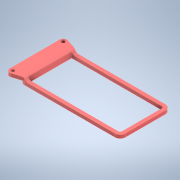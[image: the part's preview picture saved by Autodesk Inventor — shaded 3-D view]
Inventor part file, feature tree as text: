
AUTODESK INVENTOR PART (.ipt)
format: ipt  version: 2022 (Build 260153000, 153)  size: 153,600 bytes
history: native  units: mm
features: extrude x2, sketch x2, fillet x1
ambient origin geometry x8: Origin, YZ Plane, XZ Plane, XY Plane, X Axis, Y Axis, Z Axis, Center Point
bodies: Solid1 (feature_tree)
feature tree (5):
  extrude  "Extrusion1"  Depth=30.0mm
  extrude  "Extrusion2"  Depth=2.0mm
  fillet  "Fillet1"  Radius=2.0mm
  sketch  "Sketch1"  dims[d0=60.0mm d1=30.0mm]
  sketch  "Sketch2"  dims[d2=3.0mm d3=2.0mm d4=2.0mm d5=0.0mm d6=2.0mm d7=4.0mm d8=3.0mm d9=2.0mm d10=3.0mm d11=4.0mm d12=4.0mm d13=4.0mm d14=2.0mm d15=0.0mm d16=2.0mm]
